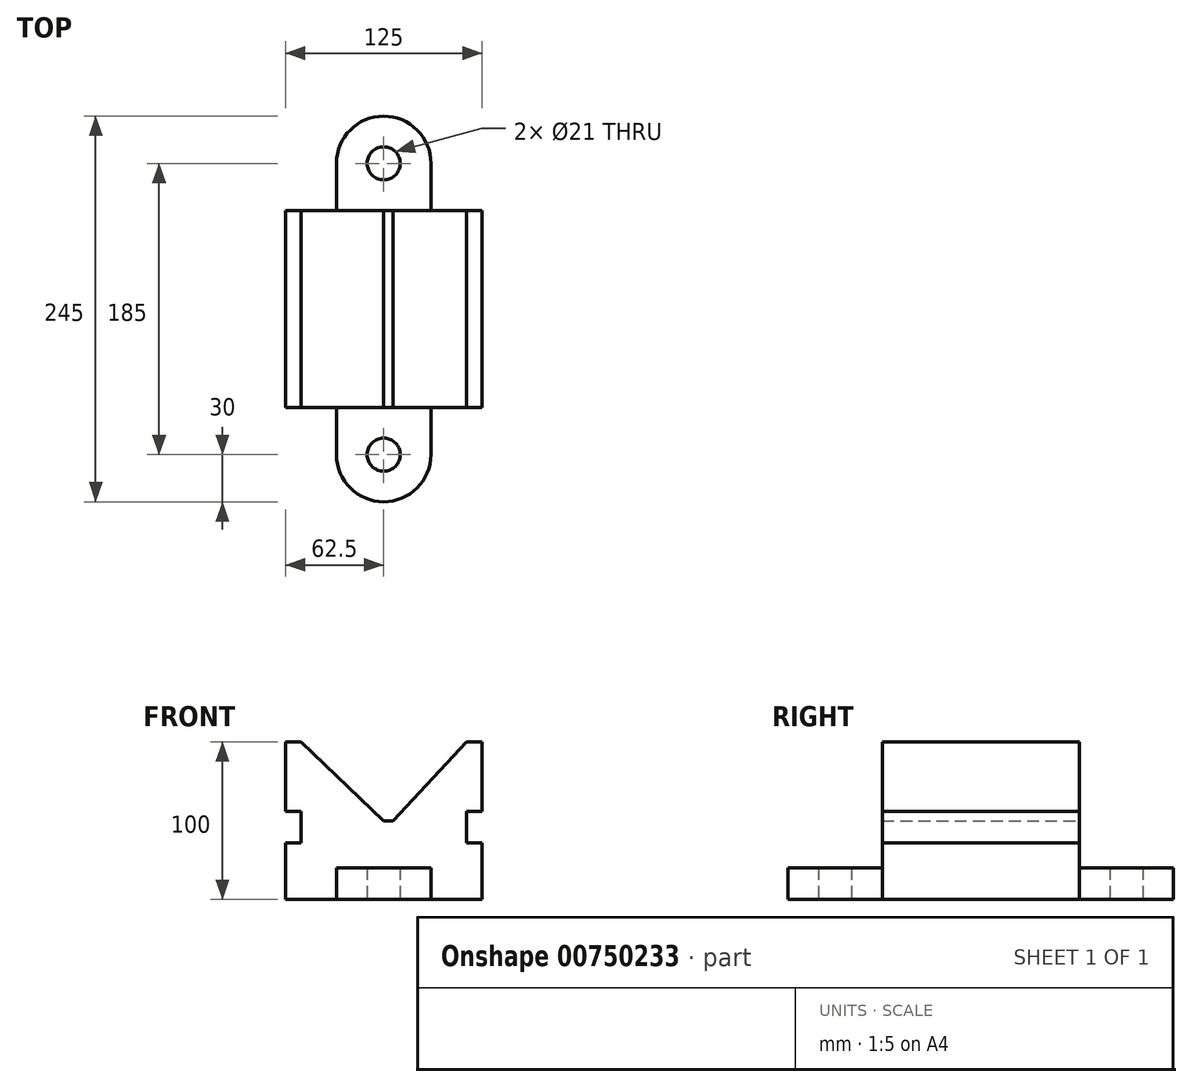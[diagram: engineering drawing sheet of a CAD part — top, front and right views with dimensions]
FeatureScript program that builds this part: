
annotation { "Feature Type Name" : "Feature", "Feature Type Description" : "" }
export const myFeature = defineFeature(function(context is Context, id is Id, definition is map)
    precondition{}
    {
        {
            var Q0;
            Q0=qCreatedBy(makeId("Front.planeOp"),FACE);
            var sketch = newSketch(context, id + "F0", { "sketchPlane" : qUnion([Q0])});
            skLineSegment(sketch, "E0", {"start": v(125, 0) * mm, "end": v(125, 36) * mm});
            skLineSegment(sketch, "E1", {"start": v(125, 36) * mm, "end": v(115, 36) * mm});
            skLineSegment(sketch, "E2", {"start": v(115, 36) * mm, "end": v(115, 56) * mm});
            skLineSegment(sketch, "E3", {"start": v(115, 56) * mm, "end": v(125, 56) * mm});
            skLineSegment(sketch, "E4", {"start": v(125, 56) * mm, "end": v(125, 100) * mm});
            skLineSegment(sketch, "E5", {"start": v(125, 100) * mm, "end": v(115, 100) * mm});
            skLineSegment(sketch, "E6", {"start": v(0, 0) * mm, "end": v(0, 36) * mm});
            skLineSegment(sketch, "E7", {"start": v(0, 36) * mm, "end": v(10, 36) * mm});
            skLineSegment(sketch, "E8", {"start": v(10, 36) * mm, "end": v(10, 56) * mm});
            skLineSegment(sketch, "E9", {"start": v(10, 56) * mm, "end": v(0, 56) * mm});
            skLineSegment(sketch, "E10", {"start": v(0, 56) * mm, "end": v(0, 100) * mm});
            skLineSegment(sketch, "E11", {"start": v(0, 100) * mm, "end": v(10, 100) * mm});
            skLineSegment(sketch, "E12", {"start": v(62.5, 50) * mm, "end": v(68.5, 50) * mm});
            skLineSegment(sketch, "E13", {"start": v(68.5, 50) * mm, "end": v(115, 100) * mm});
            skLineSegment(sketch, "E14", {"start": v(10, 100) * mm, "end": v(62.5, 50) * mm});
            skLineSegment(sketch, "E15", {"start": v(0, 0) * mm, "end": v(125, 0) * mm});
            skSolve(sketch);
        }
        {
            var Q0;
            Q0=makeQuery(id+"F0.imprint","IMPRINT",FACE,{"disambiguationData":[TD([[makeQuery(id+"F0.imprint","IMPRINT",EDGE,{"derivedFrom":sQuery(id+"F0.wireOp",EDGE,"E0")}),1.0]])]});
            extrude(context, id + "F1", {"entities" : qUnion([Q0]), "endBound" : BoundingType.SYMMETRIC, "depth" : 125 * mm, "offsetDistance" : 25 * mm});
        }
        {
            var Q0;
            Q0=qCreatedBy(makeId("Top.planeOp"),FACE);
            var sketch = newSketch(context, id + "F2", { "sketchPlane" : qUnion([Q0])});
            skLineSegment(sketch, "E16", {"start": v(32.5, -62.5) * mm, "end": v(62.5, -62.5) * mm});
            skLineSegment(sketch, "E17", {"start": v(32.5, -62.5) * mm, "end": v(32.5, -92.5) * mm});
            skLineSegment(sketch, "E18", {"start": v(92.5, -92.5) * mm, "end": v(92.5, -62.5) * mm});
            skLineSegment(sketch, "E19", {"start": v(92.5, -62.5) * mm, "end": v(62.5, -62.5) * mm});
            skArc(sketch, "E20", {"start": v(32.5, -92.5) * mm, "mid": v(62.5, -122.5) * mm, "end": v(92.5, -92.5) * mm});
            skCircle(sketch, "E21", {"center": v(62.5, -92.5) * mm, "radius": 10.5 * mm});
            skLineSegment(sketch, "E22.MirrorCS", {"start": v(32.5, 62.5) * mm, "end": v(32.5, 92.5) * mm});
            skLineSegment(sketch, "E23.MirrorCS", {"start": v(32.5, 62.5) * mm, "end": v(62.5, 62.5) * mm});
            skLineSegment(sketch, "E24.MirrorCS", {"start": v(92.5, 62.5) * mm, "end": v(62.5, 62.5) * mm});
            skLineSegment(sketch, "E25.MirrorCS", {"start": v(92.5, 92.5) * mm, "end": v(92.5, 62.5) * mm});
            skArc(sketch, "E26.MirrorCS", {"start": v(32.5, 92.5) * mm, "mid": v(62.5, 122.5) * mm, "end": v(92.5, 92.5) * mm});
            skCircle(sketch, "E27.MirrorC", {"center": v(62.5, 92.5) * mm, "radius": 10.5 * mm});
            skSolve(sketch);
        }
        {
            var Q0;
            Q0=makeQuery(id+"F2.imprint","IMPRINT",FACE,{"disambiguationData":[TD([[makeQuery(id+"F2.imprint","IMPRINT",EDGE,{"derivedFrom":sQuery(id+"F2.wireOp",EDGE,"E16")}),-1.0]])]});
            var Q1;
            Q1=makeQuery(id+"F2.imprint","IMPRINT",FACE,{"disambiguationData":[TD([[makeQuery(id+"F2.imprint","IMPRINT",EDGE,{"derivedFrom":sQuery(id+"F2.wireOp",EDGE,"E22.MirrorCS")}),-1.0]])]});
            extrude(context, id + "F3", {"entities" : qUnion([Q0, Q1]), "operationType" : NewBodyOperationType.ADD, "depth" : 20 * mm, "offsetDistance" : 25 * mm});
        }
    });
